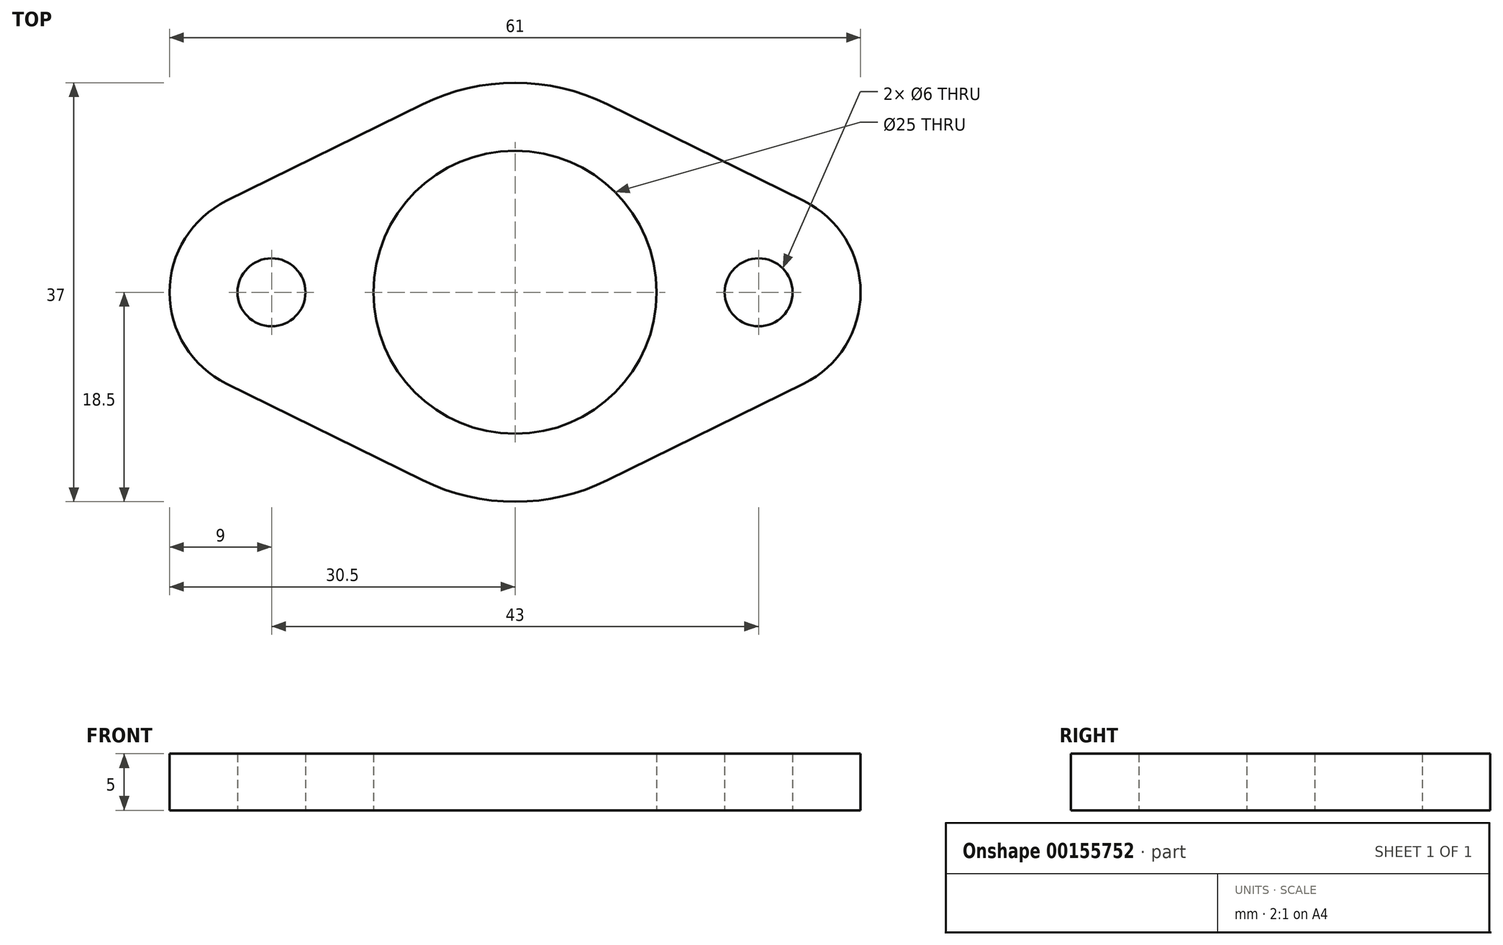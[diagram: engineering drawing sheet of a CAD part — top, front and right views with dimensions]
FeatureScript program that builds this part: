
annotation { "Feature Type Name" : "Feature", "Feature Type Description" : "" }
export const myFeature = defineFeature(function(context is Context, id is Id, definition is map)
    precondition{}
    {
        {
            var Q0;
            Q0=qCreatedBy(makeId("Top.planeOp"),FACE);
            var sketch = newSketch(context, id + "F0", { "sketchPlane" : qUnion([Q0])});
            skCircle(sketch, "E0", {"center": v(0, 0) * mm, "radius": 12.5 * mm});
            skCircle(sketch, "E1", {"center": v(-21.5, 0) * mm, "radius": 3 * mm});
            skCircle(sketch, "E2", {"center": v(21.5, 0) * mm, "radius": 3 * mm});
            skLineSegment(sketch, "E3", {"start": v(0, 30.6) * mm, "end": v(0, -26.37) * mm, "construction": true});
            skPoint(sketch, "E4", {"position": v(-18.5, 0) * mm});
            skPoint(sketch, "E5", {"position": v(-12.5, 0) * mm});
            skPoint(sketch, "E6", {"position": v(-24.5, 0) * mm});
            skPoint(sketch, "E7", {"position": v(0, 12.5) * mm});
            skArc(sketch, "E8", {"start": v(-25.48, 8.07) * mm, "mid": v(-30.5, 0) * mm, "end": v(-25.48, -8.07) * mm});
            skArc(sketch, "E9", {"start": v(25.48, -8.07) * mm, "mid": v(30.5, 0) * mm, "end": v(25.48, 8.07) * mm});
            skArc(sketch, "E10", {"start": v(-8.17, -16.6) * mm, "mid": v(0, -18.5) * mm, "end": v(8.17, -16.6) * mm});
            skLineSegment(sketch, "E11", {"start": v(-8.17, 16.6) * mm, "end": v(-25.48, 8.07) * mm});
            skLineSegment(sketch, "E12", {"start": v(-25.48, -8.07) * mm, "end": v(-8.17, -16.6) * mm});
            skLineSegment(sketch, "E13", {"start": v(25.48, -8.07) * mm, "end": v(8.17, -16.6) * mm});
            skLineSegment(sketch, "E14", {"start": v(25.48, 8.07) * mm, "end": v(8.17, 16.6) * mm});
            skArc(sketch, "E15.trimOffspring", {"start": v(8.17, 16.6) * mm, "mid": v(0, 18.5) * mm, "end": v(-8.17, 16.6) * mm});
            skSolve(sketch);
        }
        {
            var Q0;
            Q0=makeQuery(id+"F0.imprint","IMPRINT",FACE,{"disambiguationData":[TD([[makeQuery(id+"F0.imprint","IMPRINT",EDGE,{"derivedFrom":sQuery(id+"F0.wireOp",EDGE,"E0")}),-1.0]])]});
            extrude(context, id + "F1", {"entities" : qUnion([Q0]), "depth" : 5 * mm});
        }
    });
